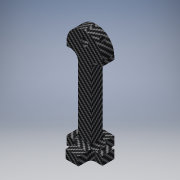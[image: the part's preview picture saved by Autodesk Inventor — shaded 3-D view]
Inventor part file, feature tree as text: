
AUTODESK INVENTOR PART (.ipt)
format: ipt  version: 2018 (Build 220112000, 112)  size: 244,736 bytes
history: native  units: mm
features: other x4, extrude x3, sketch x3, projected_geometry x3, fillet x2, reference x2
ambient origin geometry x8: Origin, YZ Plane, XZ Plane, XY Plane, X Axis, Y Axis, Z Axis, Center Point
bodies: Volumenkörper1 (feature_tree)
feature tree (17):
  extrude  "Extrusion1"  Depth=25.0mm
  extrude  "Extrusion2"  Depth=4.5mm
  extrude  "Extrusion3"  Depth=3.0mm
  fillet  "Rundung1"  Radius=75.0mm
  fillet  "Rundung2"  Radius=6.0mm
  sketch  "Skizze1"  dims[d0=9.0mm d1=25.0mm]
  reference  "Referenz1"
  sketch  "Skizze2"  dims[d2=4.5mm d3=4.5mm]
  projected_geometry  "Projizierte Kontur1"
  projected_geometry  "Projizierte Kontur2"
  sketch  "Skizze3"  dims[d4=25.0mm d5=8.0mm d6=75.0mm d7=0.0mm d8=6.0mm d9=75.0mm d10=0.0mm d12=75.0mm d13=0.0mm d14=5.2mm d15=5.0mm d16=3.0mm]
  projected_geometry  "Projizierte Kontur3"
  reference  "Referenz2"
  other  "<userpath>\OneDrive\Development\Mohne\03_Konstruktion\Mohne komplett.iam"
  other  "Mohne komplett.iam"
  other  "chassis mit motorlöcher:1"
  other  "Wheel ALL1_MIR:1"
